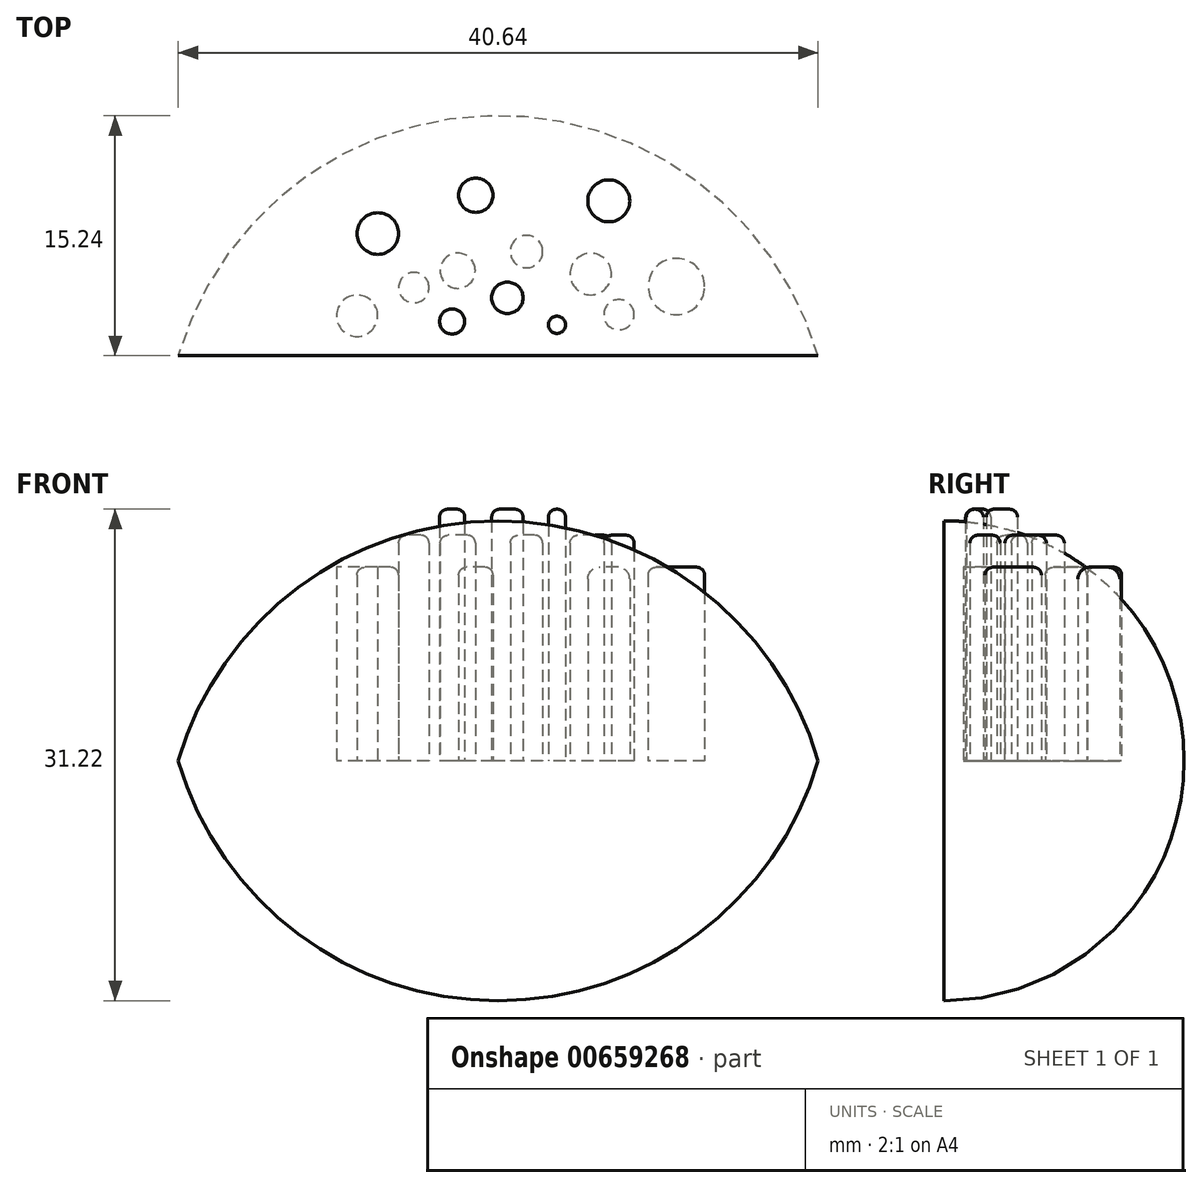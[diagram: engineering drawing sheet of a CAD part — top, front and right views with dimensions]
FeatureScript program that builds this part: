
annotation { "Feature Type Name" : "Feature", "Feature Type Description" : "" }
export const myFeature = defineFeature(function(context is Context, id is Id, definition is map)
    precondition{}
    {
        {
            var Q0;
            Q0=qCreatedBy(makeId("Front.planeOp"),FACE);
            var sketch = newSketch(context, id + "F0", { "sketchPlane" : qUnion([Q0])});
            skArc(sketch, "E0", {"start": v(20.32, 0) * mm, "mid": v(0, 15.24) * mm, "end": v(-20.32, 0) * mm});
            skLineSegment(sketch, "E1", {"start": v(20.32, 0) * mm, "end": v(-20.32, 0) * mm});
            skSolve(sketch);
        }
        {
            var Q0;
            Q0=makeQuery(id+"F0.imprint","IMPRINT",FACE,{"disambiguationData":[TD([[makeQuery(id+"F0.imprint","IMPRINT",EDGE,{"derivedFrom":sQuery(id+"F0.wireOp",EDGE,"E0")}),1.0]])]});
            var Q1;
            Q1=sQuery(id+"F0.wireOp",EDGE,"E1");
            revolve(context, id + "F1", {"entities" : qUnion([Q0]), "axis" : qUnion([Q1]), "revolveType" : RevolveType.ONE_DIRECTION, "angle" : 180 * degree});
        }
        {
            var Q0;
            Q0=qCreatedBy(makeId("Top.planeOp"),FACE);
            var sketch = newSketch(context, id + "F2", { "sketchPlane" : qUnion([Q0])});
            skCircle(sketch, "E2", {"center": v(-8.96, 2.54) * mm, "radius": 1.31 * mm});
            skCircle(sketch, "E3", {"center": v(-2.56, 5.4) * mm, "radius": 1.12 * mm});
            skCircle(sketch, "E4", {"center": v(3.73, 1.96) * mm, "radius": 0.55 * mm});
            skCircle(sketch, "E5", {"center": v(1.8, 6.61) * mm, "radius": 1.02 * mm});
            skCircle(sketch, "E6", {"center": v(-2.92, 2.17) * mm, "radius": 0.8 * mm});
            skCircle(sketch, "E7", {"center": v(-7.65, 7.76) * mm, "radius": 1.32 * mm});
            skCircle(sketch, "E8", {"center": v(7.03, 9.83) * mm, "radius": 1.33 * mm});
            skCircle(sketch, "E9", {"center": v(5.88, 5.18) * mm, "radius": 1.32 * mm});
            skCircle(sketch, "E10", {"center": v(-1.42, 10.19) * mm, "radius": 1.1 * mm});
            skCircle(sketch, "E11", {"center": v(11.32, 4.4) * mm, "radius": 1.79 * mm});
            skCircle(sketch, "E12", {"center": v(7.67, 2.6) * mm, "radius": 0.96 * mm});
            skCircle(sketch, "E13", {"center": v(0.58, 3.68) * mm, "radius": 1 * mm});
            skCircle(sketch, "E14", {"center": v(-5.36, 4.32) * mm, "radius": 0.96 * mm});
            skSolve(sketch);
        }
        {
            var Q0;
            Q0=makeQuery(id+"F2.imprint","IMPRINT",FACE,{"disambiguationData":[TD([[makeQuery(id+"F2.imprint","IMPRINT",EDGE,{"derivedFrom":sQuery(id+"F2.wireOp",EDGE,"E4")}),1.0]])]});
            var Q1;
            Q1=makeQuery(id+"F2.imprint","IMPRINT",FACE,{"disambiguationData":[TD([[makeQuery(id+"F2.imprint","IMPRINT",EDGE,{"derivedFrom":sQuery(id+"F2.wireOp",EDGE,"E13")}),1.0]])]});
            var Q2;
            Q2=makeQuery(id+"F2.imprint","IMPRINT",FACE,{"disambiguationData":[TD([[makeQuery(id+"F2.imprint","IMPRINT",EDGE,{"derivedFrom":sQuery(id+"F2.wireOp",EDGE,"E6")}),1.0]])]});
            extrude(context, id + "F3", {"entities" : qUnion([Q0, Q1, Q2]), "depth" : 15.98 * mm, "offsetDistance" : 25.4 * mm});
        }
        {
            var Q0;
            Q0=makeQuery(id+"F2.imprint","IMPRINT",FACE,{"disambiguationData":[TD([[makeQuery(id+"F2.imprint","IMPRINT",EDGE,{"derivedFrom":sQuery(id+"F2.wireOp",EDGE,"E9")}),1.0]])]});
            var Q1;
            Q1=makeQuery(id+"F2.imprint","IMPRINT",FACE,{"disambiguationData":[TD([[makeQuery(id+"F2.imprint","IMPRINT",EDGE,{"derivedFrom":sQuery(id+"F2.wireOp",EDGE,"E5")}),1.0]])]});
            var Q2;
            Q2=makeQuery(id+"F2.imprint","IMPRINT",FACE,{"disambiguationData":[TD([[makeQuery(id+"F2.imprint","IMPRINT",EDGE,{"derivedFrom":sQuery(id+"F2.wireOp",EDGE,"E12")}),1.0]])]});
            var Q3;
            Q3=makeQuery(id+"F2.imprint","IMPRINT",FACE,{"disambiguationData":[TD([[makeQuery(id+"F2.imprint","IMPRINT",EDGE,{"derivedFrom":sQuery(id+"F2.wireOp",EDGE,"E3")}),1.0]])]});
            var Q4;
            Q4=makeQuery(id+"F2.imprint","IMPRINT",FACE,{"disambiguationData":[TD([[makeQuery(id+"F2.imprint","IMPRINT",EDGE,{"derivedFrom":sQuery(id+"F2.wireOp",EDGE,"E14")}),1.0]])]});
            extrude(context, id + "F4", {"entities" : qUnion([Q0, Q1, Q2, Q3, Q4]), "depth" : 14.33 * mm, "offsetDistance" : 25.4 * mm});
        }
        {
            var Q0;
            Q0=makeQuery(id+"F2.imprint","IMPRINT",FACE,{"disambiguationData":[TD([[makeQuery(id+"F2.imprint","IMPRINT",EDGE,{"derivedFrom":sQuery(id+"F2.wireOp",EDGE,"E10")}),1.0]])]});
            var Q1;
            Q1=makeQuery(id+"F2.imprint","IMPRINT",FACE,{"disambiguationData":[TD([[makeQuery(id+"F2.imprint","IMPRINT",EDGE,{"derivedFrom":sQuery(id+"F2.wireOp",EDGE,"E8")}),1.0]])]});
            var Q2;
            Q2=makeQuery(id+"F2.imprint","IMPRINT",FACE,{"disambiguationData":[TD([[makeQuery(id+"F2.imprint","IMPRINT",EDGE,{"derivedFrom":sQuery(id+"F2.wireOp",EDGE,"E11")}),1.0]])]});
            var Q3;
            Q3=makeQuery(id+"F2.imprint","IMPRINT",FACE,{"disambiguationData":[TD([[makeQuery(id+"F2.imprint","IMPRINT",EDGE,{"derivedFrom":sQuery(id+"F2.wireOp",EDGE,"E7")}),1.0]])]});
            var Q4;
            Q4=makeQuery(id+"F2.imprint","IMPRINT",FACE,{"disambiguationData":[TD([[makeQuery(id+"F2.imprint","IMPRINT",EDGE,{"derivedFrom":sQuery(id+"F2.wireOp",EDGE,"E2")}),1.0]])]});
            extrude(context, id + "F5", {"entities" : qUnion([Q0, Q1, Q2, Q3, Q4]), "depth" : 12.3 * mm, "offsetDistance" : 25.4 * mm});
        }
        {
            var Q0;
            Q0=makeQuery(id+"F5.opExtrude","CAP_FACE",FACE,{"disambiguationData":[OSD([sQuery(id+"F2.wireOp",EDGE,"E11")])],"isStart":false});
            var Q1;
            Q1=makeQuery(id+"F4.opExtrude","CAP_FACE",FACE,{"disambiguationData":[OSD([sQuery(id+"F2.wireOp",EDGE,"E9")])],"isStart":false});
            var Q2;
            Q2=makeQuery(id+"F4.opExtrude","CAP_EDGE",EDGE,{"disambiguationData":[OSD([sQuery(id+"F2.wireOp",EDGE,"E12")])],"isStart":false});
            var Q3;
            Q3=makeQuery(id+"F3.opExtrude","CAP_EDGE",EDGE,{"disambiguationData":[OSD([sQuery(id+"F2.wireOp",EDGE,"E4")])],"isStart":false});
            var Q4;
            Q4=makeQuery(id+"F3.opExtrude","CAP_FACE",FACE,{"disambiguationData":[OSD([sQuery(id+"F2.wireOp",EDGE,"E13")])],"isStart":false});
            var Q5;
            Q5=makeQuery(id+"F4.opExtrude","CAP_FACE",FACE,{"disambiguationData":[OSD([sQuery(id+"F2.wireOp",EDGE,"E5")])],"isStart":false});
            var Q6;
            Q6=makeQuery(id+"F5.opExtrude","CAP_EDGE",EDGE,{"disambiguationData":[OSD([sQuery(id+"F2.wireOp",EDGE,"E10")])],"isStart":false});
            var Q7;
            Q7=makeQuery(id+"F4.opExtrude","CAP_EDGE",EDGE,{"disambiguationData":[OSD([sQuery(id+"F2.wireOp",EDGE,"E3")])],"isStart":false});
            var Q8;
            Q8=makeQuery(id+"F4.opExtrude","CAP_EDGE",EDGE,{"disambiguationData":[OSD([sQuery(id+"F2.wireOp",EDGE,"E14")])],"isStart":false});
            var Q9;
            Q9=makeQuery(id+"F3.opExtrude","CAP_FACE",FACE,{"disambiguationData":[OSD([sQuery(id+"F2.wireOp",EDGE,"E6")])],"isStart":false});
            var Q10;
            Q10=makeQuery(id+"F5.opExtrude","CAP_FACE",FACE,{"disambiguationData":[OSD([sQuery(id+"F2.wireOp",EDGE,"E7")])],"isStart":false});
            fillet(context, id + "F6", {"entities" : qUnion([Q0, Q1, Q2, Q3, Q4, Q5, Q6, Q7, Q8, Q9, Q10]), "radius" : 0.5 * mm, "tangentPropagation" : true, "allowEdgeOverflow" : false});
        }
        {
            var Q0;
            Q0=makeQuery(id+"F6.opFillet","BLEND_FACE",FACE,{"disambiguationData":[OSD([sQuery(id+"F2.wireOp",EDGE,"E11")])]});
            var Q1;
            Q1=makeQuery(id+"F6.opFillet","BLEND_FACE",FACE,{"disambiguationData":[OSD([sQuery(id+"F2.wireOp",EDGE,"E9")])]});
            var Q2;
            Q2=makeQuery(id+"F5.opExtrude","CAP_FACE",FACE,{"disambiguationData":[OSD([sQuery(id+"F2.wireOp",EDGE,"E8")])],"isStart":false});
            var Q3;
            Q3=makeQuery(id+"F6.opFillet","BLEND_FACE",FACE,{"disambiguationData":[OSD([sQuery(id+"F2.wireOp",EDGE,"E10")])]});
            var Q4;
            {var subQ0=sQuery(id+"F2.wireOp",EDGE,"E7");Q4=makeQuery(id+"F6.opFillet","BLEND_EDGE",EDGE,{"blendedFrom":[makeQuery(id+"F5.opExtrude","CAP_EDGE",EDGE,{"disambiguationData":[OSD([subQ0])],"isStart":false}),makeQuery(id+"F5.opExtrude","SWEPT_FACE",FACE,{"disambiguationData":[OSD([subQ0])]})],"blendedInto":[makeQuery(id+"F5.opExtrude","SWEPT_FACE",FACE,{"disambiguationData":[OSD([subQ0])]})]});}
            var Q5;
            {var subQ0=sQuery(id+"F2.wireOp",EDGE,"E7");Q5=makeQuery(id+"F6.opFillet","BLEND_EDGE",EDGE,{"blendedFrom":[makeQuery(id+"F5.opExtrude","CAP_EDGE",EDGE,{"disambiguationData":[OSD([subQ0])],"isStart":false}),makeQuery(id+"F5.opExtrude","CAP_FACE",FACE,{"disambiguationData":[OSD([subQ0])],"isStart":false})],"blendedInto":[makeQuery(id+"F5.opExtrude","CAP_FACE",FACE,{"disambiguationData":[OSD([subQ0])],"isStart":false})]});}
            fillet(context, id + "F7", {"entities" : qUnion([Q0, Q1, Q2, Q3, Q4, Q5]), "radius" : 0.76 * mm, "tangentPropagation" : true, "allowEdgeOverflow" : false});
        }
    });
